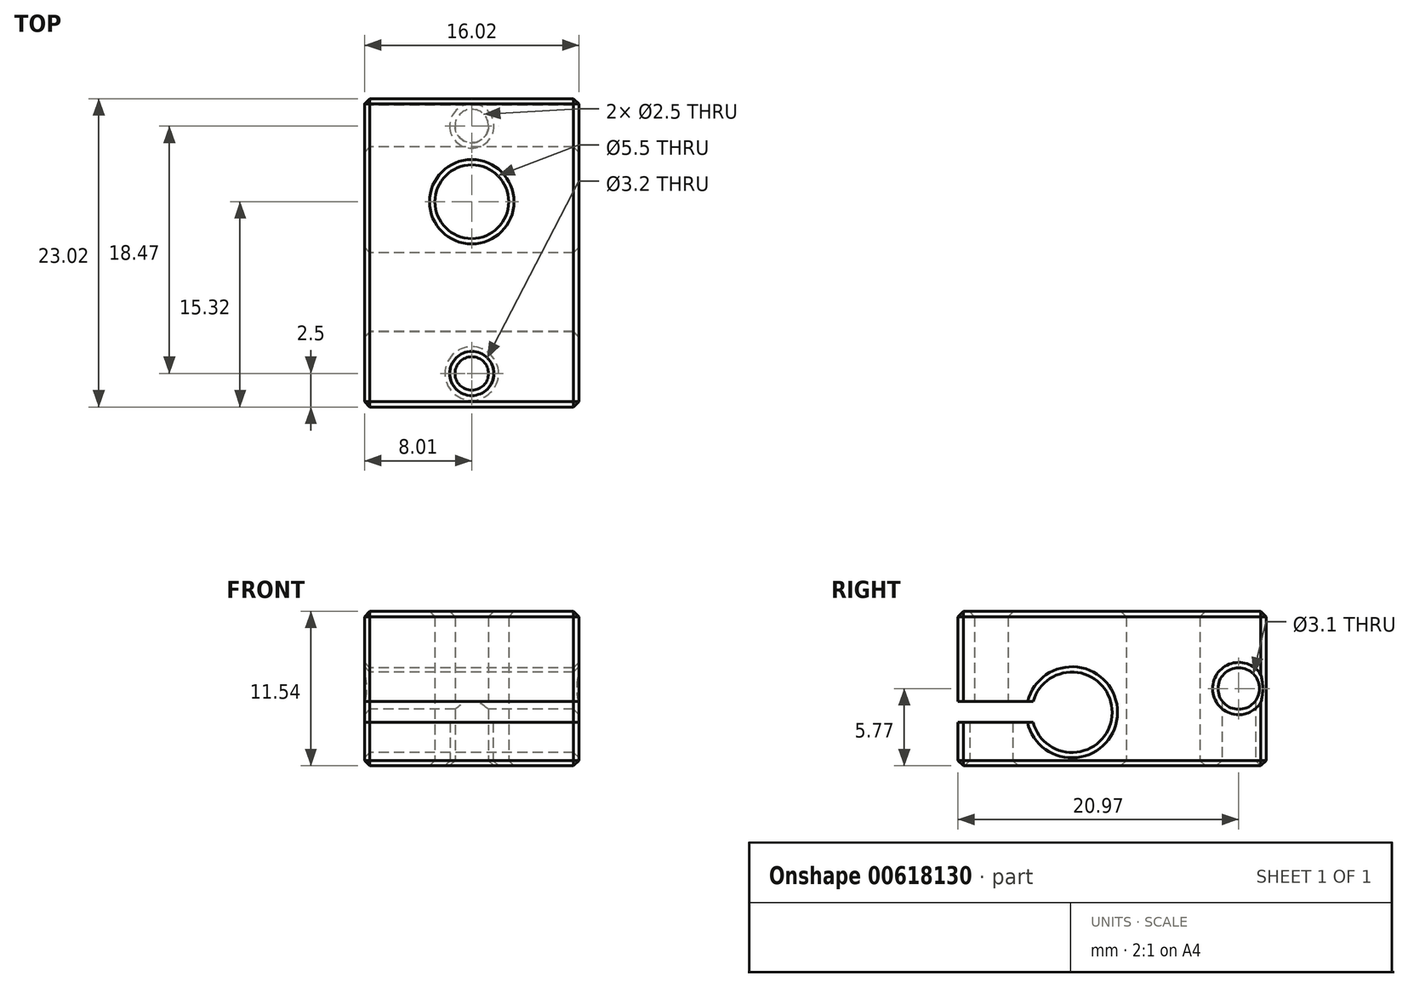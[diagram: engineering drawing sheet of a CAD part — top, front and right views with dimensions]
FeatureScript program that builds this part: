
annotation { "Feature Type Name" : "Feature", "Feature Type Description" : "" }
export const myFeature = defineFeature(function(context is Context, id is Id, definition is map)
    precondition{}
    {
        {
            var Q0;
            Q0=qCreatedBy(makeId("Right.planeOp"),FACE);
            var sketch = newSketch(context, id + "F0", { "sketchPlane" : qUnion([Q0])});
            skLineSegment(sketch, "E0.bottom", {"start": v(11.5, 5.77) * mm, "end": v(-11.5, 5.77) * mm});
            skLineSegment(sketch, "E0.top", {"start": v(11.5, -5.77) * mm, "end": v(-11.5, -5.77) * mm});
            skLineSegment(sketch, "E0.left", {"start": v(11.5, 5.77) * mm, "end": v(11.5, -5.77) * mm});
            skLineSegment(sketch, "E0.right", {"start": v(-11.5, 5.77) * mm, "end": v(-11.5, -5.77) * mm});
            skPoint(sketch, "E0.middle", {"position": v(0, 0) * mm});
            skLineSegment(sketch, "E1", {"start": v(-11.5, -0.97) * mm, "end": v(-5.88, -0.97) * mm});
            skLineSegment(sketch, "E2", {"start": v(-11.5, -2.52) * mm, "end": v(-5.9, -2.52) * mm});
            skCircle(sketch, "E3", {"center": v(-3, -1.77) * mm, "radius": 3 * mm});
            skCircle(sketch, "E4", {"center": v(9.46, 0) * mm, "radius": 1.55 * mm});
            skPoint(sketch, "E5", {"position": v(11.5, 0) * mm});
            skSolve(sketch);
        }
        {
            var Q0;
            Q0=makeQuery(id+"F0.imprint","IMPRINT",FACE,{"disambiguationData":[TD([[makeQuery(id+"F0.imprint","IMPRINT",EDGE,{"derivedFrom":sQuery(id+"F0.wireOp",EDGE,"E0.bottom")}),1.0]])]});
            extrude(context, id + "F1", {"entities" : qUnion([Q0]), "endBound" : BoundingType.SYMMETRIC, "depth" : 16.01 * mm, "offsetDistance" : 25 * mm});
        }
        {
            var Q0;
            Q0=makeQuery(id+"F1.opExtrude","SWEPT_FACE",FACE,{"disambiguationData":[OSD([sQuery(id+"F0.wireOp",EDGE,"E0.top")])]});
            var sketch = newSketch(context, id + "F2", { "sketchPlane" : qUnion([Q0])});
            skPoint(sketch, "E6", {"position": v(0, 9) * mm});
            skPoint(sketch, "E7", {"position": v(0, -9.46) * mm});
            skPoint(sketch, "E8", {"position": v(0, -3.8) * mm});
            skSolve(sketch);
        }
        {
            var Q0;
            Q0=sQuery(id+"F2.wireOp",VERTEX,"E8");
            var Q1;
            Q1=makeQuery(id+"F1.opExtrude","SWEPT_BODY",BODY,{"disambiguationData":[OSD([sQuery(id+"F0.wireOp",EDGE,"E0.bottom"),sQuery(id+"F0.wireOp",EDGE,"E0.top"),sQuery(id+"F0.wireOp",EDGE,"E0.left"),sQuery(id+"F0.wireOp",EDGE,"E0.right"),sQuery(id+"F0.wireOp",EDGE,"E1"),sQuery(id+"F0.wireOp",EDGE,"E2"),sQuery(id+"F0.wireOp",EDGE,"E3"),sQuery(id+"F0.wireOp",EDGE,"E4")])]});
            hole(context, id + "F3", {"style" : HoleStyle.SIMPLE, "endStyle" : HoleEndStyle.THROUGH, "standardTappedOrClearance" : lookupTablePath({ "standard" : "ISO", "fit" : "Normal", "size" : "M5", "type" : "Clearance" }), "standardBlindInLast" : lookupTablePath({ "fit" : "Standard", "standard" : "ISO", "size" : "M5", "type" : "Clearance" }), "holeDiameter" : 5.5 * mm, "majorDiameter" : 5 * mm, "isTappedThrough" : true, "tappedDepth" : 12 * mm, "tapClearance" : 3, "locations" : qUnion([Q0]), "scope" : qUnion([Q1])});
        }
        {
            var Q0;
            Q0=sQuery(id+"F2.wireOp",VERTEX,"E6");
            var Q1;
            Q1=makeQuery(id+"F1.opExtrude","SWEPT_BODY",BODY,{"disambiguationData":[OSD([sQuery(id+"F0.wireOp",EDGE,"E0.bottom"),sQuery(id+"F0.wireOp",EDGE,"E0.top"),sQuery(id+"F0.wireOp",EDGE,"E0.left"),sQuery(id+"F0.wireOp",EDGE,"E0.right"),sQuery(id+"F0.wireOp",EDGE,"E1"),sQuery(id+"F0.wireOp",EDGE,"E2"),sQuery(id+"F0.wireOp",EDGE,"E3"),sQuery(id+"F0.wireOp",EDGE,"E4")])]});
            hole(context, id + "F4", {"style" : HoleStyle.C_BORE, "endStyle" : HoleEndStyle.THROUGH, "holeDiameter" : 2.5 * mm, "cBoreDiameter" : 3.2 * mm, "cBoreDepth" : 4.6 * mm, "majorDiameter" : 3 * mm, "isTappedThrough" : true, "tappedDepth" : 12 * mm, "tapClearance" : 3, "locations" : qUnion([Q0]), "scope" : qUnion([Q1])});
        }
        {
            var Q0;
            Q0=sQuery(id+"F2.wireOp",VERTEX,"E7");
            var Q1;
            Q1=makeQuery(id+"F1.opExtrude","SWEPT_BODY",BODY,{"disambiguationData":[OSD([sQuery(id+"F0.wireOp",EDGE,"E0.bottom"),sQuery(id+"F0.wireOp",EDGE,"E0.top"),sQuery(id+"F0.wireOp",EDGE,"E0.left"),sQuery(id+"F0.wireOp",EDGE,"E0.right"),sQuery(id+"F0.wireOp",EDGE,"E1"),sQuery(id+"F0.wireOp",EDGE,"E2"),sQuery(id+"F0.wireOp",EDGE,"E3"),sQuery(id+"F0.wireOp",EDGE,"E4")])]});
            hole(context, id + "F5", {"style" : HoleStyle.SIMPLE, "endStyle" : HoleEndStyle.BLIND, "holeDiameter" : 2.5 * mm, "majorDiameter" : 5 * mm, "holeDepth" : 5 * mm, "isTappedThrough" : true, "tappedDepth" : 12 * mm, "tapClearance" : 3, "locations" : qUnion([Q0]), "scope" : qUnion([Q1])});
        }
        {
            var Q0;
            Q0=makeQuery(id+"F1.opExtrude","SWEPT_FACE",FACE,{"disambiguationData":[OSD([sQuery(id+"F0.wireOp",EDGE,"E0.top")])]});
            var Q1;
            Q1=makeQuery(id+"F1.opExtrude","SWEPT_FACE",FACE,{"disambiguationData":[OSD([sQuery(id+"F0.wireOp",EDGE,"E0.bottom")])]});
            var Q2;
            Q2=makeQuery(id+"F1.opExtrude","CAP_EDGE",EDGE,{"disambiguationData":[OSD([sQuery(id+"F0.wireOp",EDGE,"E3")])],"isStart":true});
            var Q3;
            Q3=makeQuery(id+"F1.opExtrude","CAP_EDGE",EDGE,{"disambiguationData":[OSD([sQuery(id+"F0.wireOp",EDGE,"E4")])],"isStart":true});
            var Q4;
            {var subQ0=sQuery(id+"F0.wireOp",EDGE,"E0.right");Q4=makeQuery(id+"F1.opExtrude","CAP_EDGE",EDGE,{"disambiguationData":[OSD([subQ0]),TDD([makeQuery(id+"F0.imprint","IMPRINT",EDGE,{"disambiguationData":[TD([[makeQuery(id+"F0.imprint","INTERSECT",VERTEX,{"derivedFrom":[sQuery(id+"F0.wireOp",EDGE,"E0.top"),subQ0]}),1.0]])],"derivedFrom":subQ0})])],"isStart":true});}
            var Q5;
            {var subQ0=sQuery(id+"F0.wireOp",EDGE,"E0.right");Q5=makeQuery(id+"F1.opExtrude","CAP_EDGE",EDGE,{"disambiguationData":[OSD([subQ0]),TDD([makeQuery(id+"F0.imprint","IMPRINT",EDGE,{"disambiguationData":[TD([[makeQuery(id+"F0.imprint","INTERSECT",VERTEX,{"derivedFrom":[sQuery(id+"F0.wireOp",EDGE,"E0.bottom"),subQ0]}),-1.0]])],"derivedFrom":subQ0})])],"isStart":true});}
            var Q6;
            Q6=makeQuery(id+"F1.opExtrude","SWEPT_FACE",FACE,{"disambiguationData":[OSD([sQuery(id+"F0.wireOp",EDGE,"E0.left")])]});
            var Q7;
            Q7=makeQuery(id+"F1.opExtrude","CAP_EDGE",EDGE,{"disambiguationData":[OSD([sQuery(id+"F0.wireOp",EDGE,"E4")])],"isStart":false});
            var Q8;
            Q8=makeQuery(id+"F1.opExtrude","CAP_EDGE",EDGE,{"disambiguationData":[OSD([sQuery(id+"F0.wireOp",EDGE,"E3")])],"isStart":false});
            var Q9;
            {var subQ0=sQuery(id+"F0.wireOp",EDGE,"E0.right");Q9=makeQuery(id+"F1.opExtrude","CAP_EDGE",EDGE,{"disambiguationData":[OSD([subQ0]),TDD([makeQuery(id+"F0.imprint","IMPRINT",EDGE,{"disambiguationData":[TD([[makeQuery(id+"F0.imprint","INTERSECT",VERTEX,{"derivedFrom":[sQuery(id+"F0.wireOp",EDGE,"E0.bottom"),subQ0]}),-1.0]])],"derivedFrom":subQ0})])],"isStart":false});}
            var Q10;
            {var subQ0=sQuery(id+"F0.wireOp",EDGE,"E0.right");Q10=makeQuery(id+"F1.opExtrude","CAP_EDGE",EDGE,{"disambiguationData":[OSD([subQ0]),TDD([makeQuery(id+"F0.imprint","IMPRINT",EDGE,{"disambiguationData":[TD([[makeQuery(id+"F0.imprint","INTERSECT",VERTEX,{"derivedFrom":[sQuery(id+"F0.wireOp",EDGE,"E0.top"),subQ0]}),1.0]])],"derivedFrom":subQ0})])],"isStart":false});}
            chamfer(context, id + "F6", {"entities" : qUnion([Q0, Q1, Q2, Q3, Q4, Q5, Q6, Q7, Q8, Q9, Q10]), "width" : 0.4 * mm, "tangentPropagation" : true});
        }
    });
